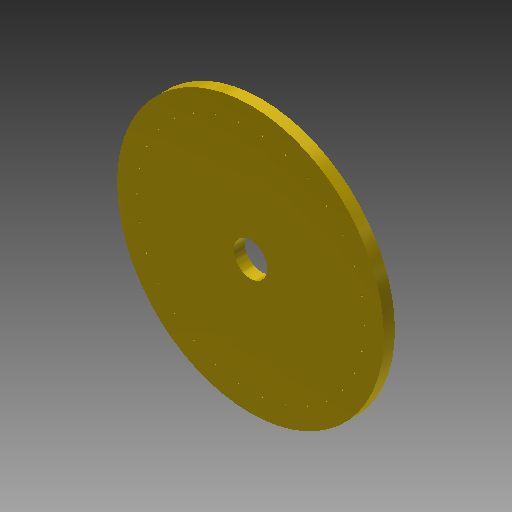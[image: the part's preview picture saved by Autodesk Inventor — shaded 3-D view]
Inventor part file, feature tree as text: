
AUTODESK INVENTOR PART (.ipt)
format: ipt  version: 2017 (Build 210142000, 142)  size: 155,648 bytes
history: native  units: mm (DEFAULTED — no unit token found)
features: sketch x3, revolve x2, pattern_circular x2, projected_geometry x2, extrude x1
ambient origin geometry x8: Origin, YZ Plane, XZ Plane, XY Plane, X Axis, Y Axis, Z Axis, Center Point
bodies: Solid1 (feature_tree)
feature tree (10):
  extrude  "Extrusion1"  Depth=241.3mm
  revolve  "Revolution1"  Angle=90.0deg
  pattern_circular  "Circular Pattern1"  Count=30 Angle=360.0deg
  revolve  "Revolution2"  [1 undecoded]
  pattern_circular  "Circular Pattern2"  [2 undecoded]
  sketch  "Sketch1"  dims[d0=30.5mm d1=241.3mm]
  sketch  "Sketch2"  dims[d2=10.0mm d3=0.0mm d7=90.0deg d8=300.0mm d9=360.0deg]
  projected_geometry  "Projected Loop1"
  projected_geometry  "Projected Loop2"
  sketch  "Sketch3"  dims[d11=1.5mm d12=0.5mm d13=2.0mm d14=90.0deg d15=80.0mm d16=360.0deg d18=2.0mm d19=0.5mm d20=102.85mm]
note: 3 required parameter values undecoded (feature->parameter linkage not recoverable at this tier; creation-order binding heuristic only, values carry confidence <= 0.55)